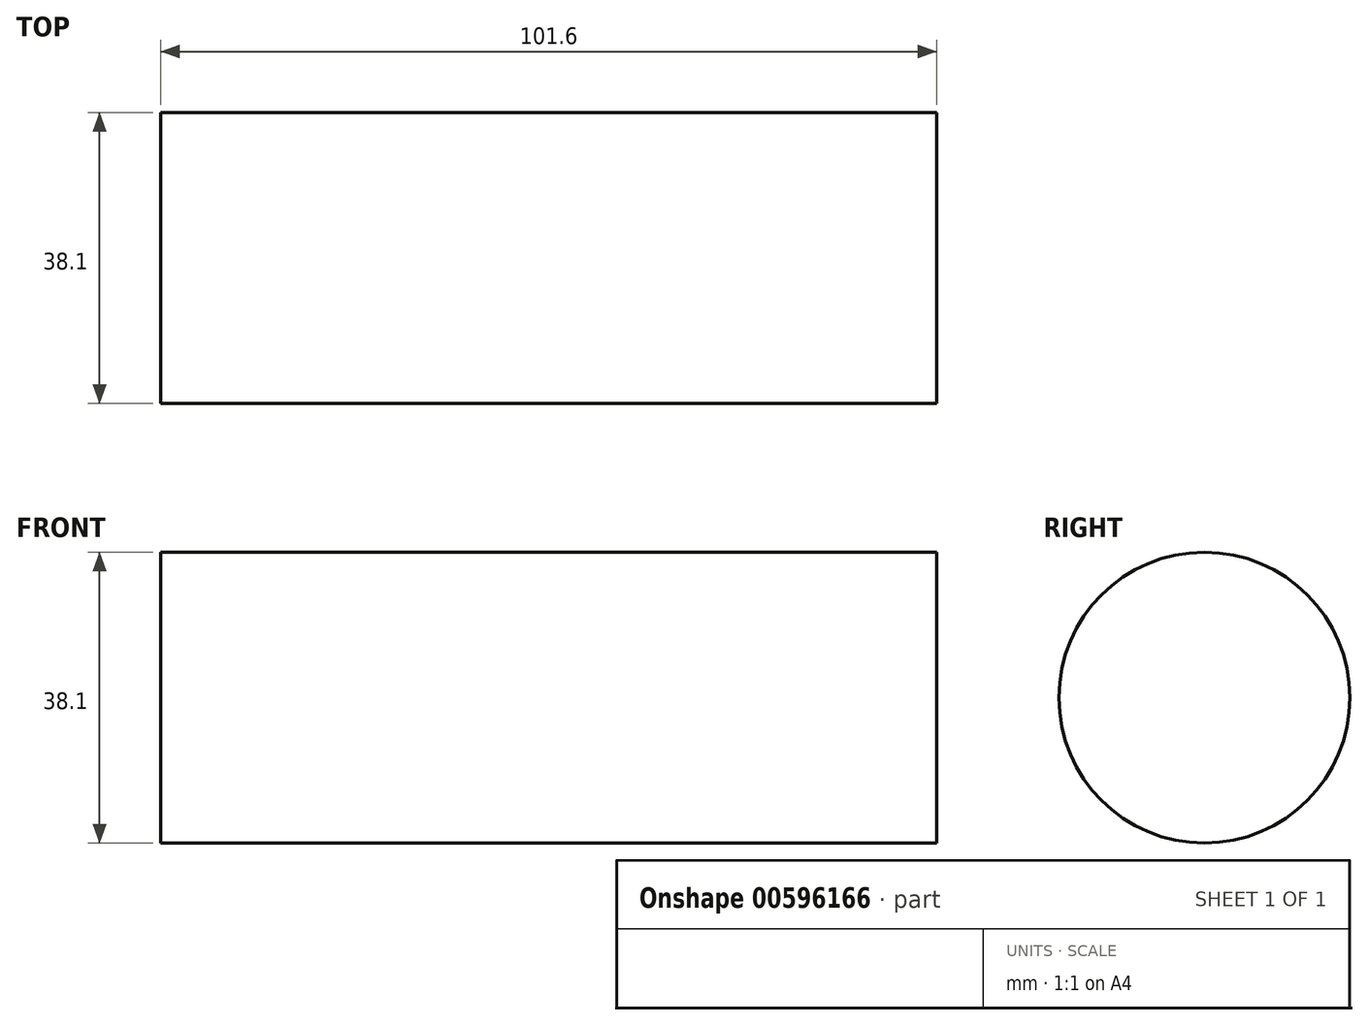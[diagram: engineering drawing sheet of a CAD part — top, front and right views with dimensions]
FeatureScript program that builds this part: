
annotation { "Feature Type Name" : "Feature", "Feature Type Description" : "" }
export const myFeature = defineFeature(function(context is Context, id is Id, definition is map)
    precondition{}
    {
        {
            var Q0;
            Q0=qCreatedBy(makeId("Front.planeOp"),FACE);
            var sketch = newSketch(context, id + "F0", { "sketchPlane" : qUnion([Q0])});
            skLineSegment(sketch, "E0.bottom", {"start": v(25.5, -17.68) * mm, "end": v(-76.1, -17.68) * mm});
            skLineSegment(sketch, "E0.top", {"start": v(25.5, -36.73) * mm, "end": v(-76.1, -36.73) * mm});
            skLineSegment(sketch, "E0.left", {"start": v(25.5, -17.68) * mm, "end": v(25.5, -36.73) * mm});
            skLineSegment(sketch, "E0.right", {"start": v(-76.1, -17.68) * mm, "end": v(-76.1, -36.73) * mm});
            skLineSegment(sketch, "E1.bottom", {"start": v(25.5, -36.73) * mm, "end": v(31.85, -36.73) * mm});
            skLineSegment(sketch, "E1.top", {"start": v(25.5, -4.98) * mm, "end": v(31.85, -4.98) * mm});
            skLineSegment(sketch, "E1.left", {"start": v(25.5, -36.73) * mm, "end": v(25.5, -4.98) * mm});
            skLineSegment(sketch, "E1.right", {"start": v(31.85, -36.73) * mm, "end": v(31.85, -4.98) * mm});
            skLineSegment(sketch, "E2.bottom", {"start": v(31.85, -4.98) * mm, "end": v(44.55, -4.98) * mm});
            skLineSegment(sketch, "E2.top", {"start": v(31.85, -8.15) * mm, "end": v(44.55, -8.15) * mm});
            skLineSegment(sketch, "E2.left", {"start": v(31.85, -4.98) * mm, "end": v(31.85, -8.15) * mm});
            skLineSegment(sketch, "E2.right", {"start": v(44.55, -4.98) * mm, "end": v(44.55, -8.15) * mm});
            skSolve(sketch);
        }
        {
            var Q0;
            {var subQ0=sQuery(id+"F0.wireOp",EDGE,"E0.bottom");Q0=makeQuery(id+"F0.imprint","IMPRINT",FACE,{"disambiguationData":[TD([[makeQuery(id+"F0.imprint","IMPRINT",EDGE,{"derivedFrom":subQ0}),1.0]])]});}
            var Q1;
            Q1=sQuery(id+"F0.wireOp",EDGE,"E0.top");
            revolve(context, id + "F1", {"entities" : qUnion([Q0]), "axis" : qUnion([Q1]), "revolveType" : RevolveType.FULL});
        }
    });
